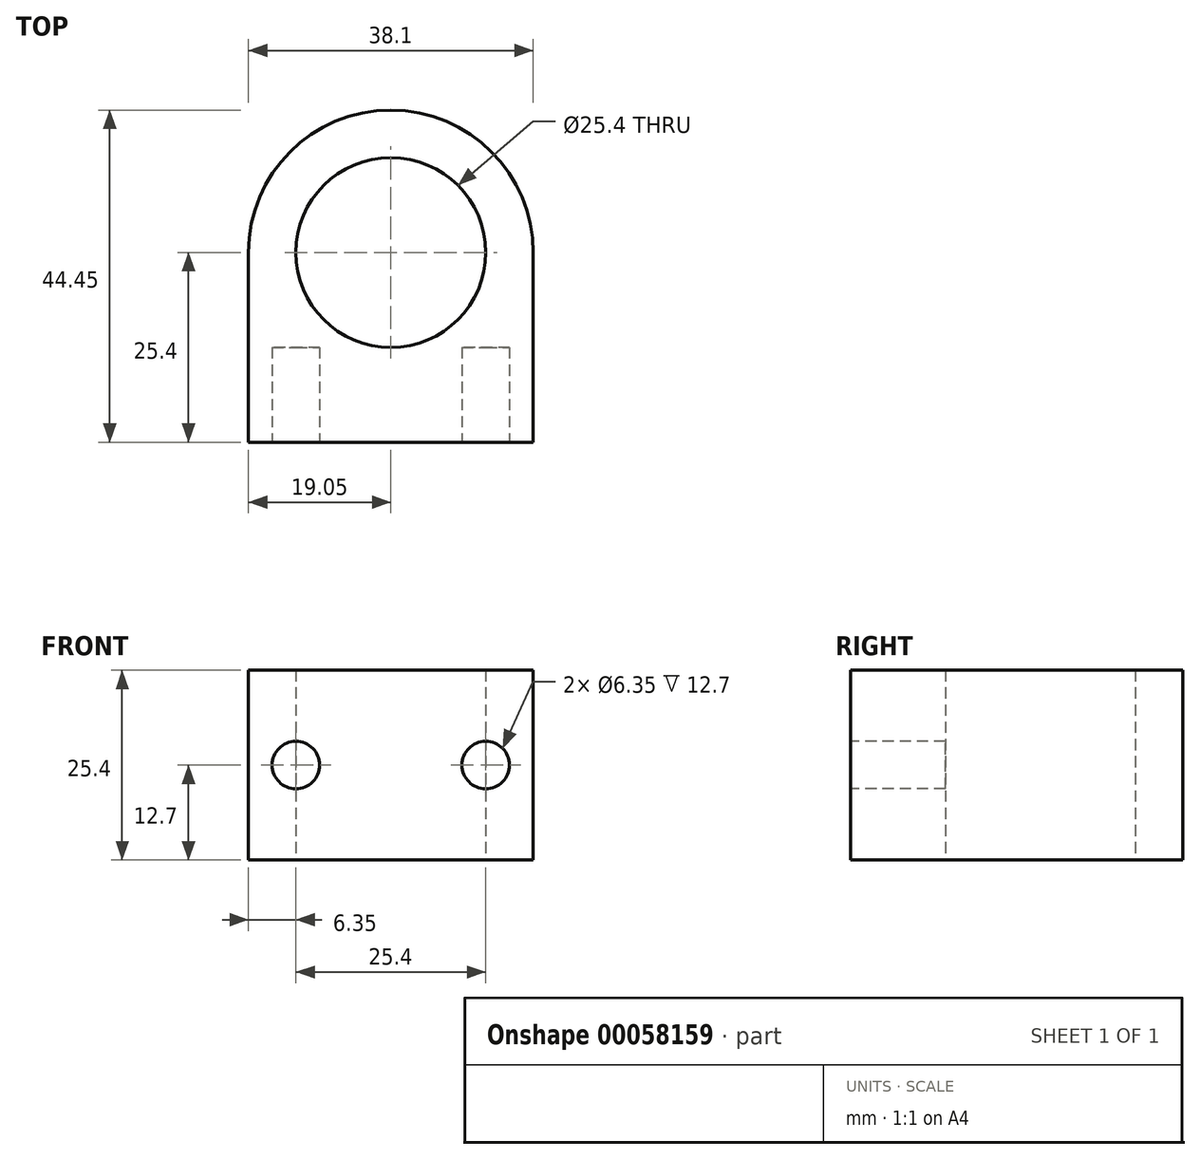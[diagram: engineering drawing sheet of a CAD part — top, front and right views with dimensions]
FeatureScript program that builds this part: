
annotation { "Feature Type Name" : "Feature", "Feature Type Description" : "" }
export const myFeature = defineFeature(function(context is Context, id is Id, definition is map)
    precondition{}
    {
        {
            var Q0;
            Q0=qCreatedBy(makeId("Top.planeOp"),FACE);
            var sketch = newSketch(context, id + "F0", { "sketchPlane" : qUnion([Q0])});
            skCircle(sketch, "E0", {"center": v(0, 0) * mm, "radius": 12.7 * mm});
            skArc(sketch, "E1", {"start": v(19.05, 0) * mm, "mid": v(0, 19.05) * mm, "end": v(-19.05, 0) * mm});
            skLineSegment(sketch, "E2", {"start": v(-19.05, 0) * mm, "end": v(-19.05, -25.4) * mm});
            skLineSegment(sketch, "E3", {"start": v(-19.05, -25.4) * mm, "end": v(19.05, -25.4) * mm});
            skLineSegment(sketch, "E4", {"start": v(19.05, -25.4) * mm, "end": v(19.05, 0) * mm});
            skSolve(sketch);
        }
        {
            var Q0;
            Q0=makeQuery(id+"F0.imprint","IMPRINT",FACE,{"disambiguationData":[TD([[makeQuery(id+"F0.imprint","IMPRINT",EDGE,{"derivedFrom":sQuery(id+"F0.wireOp",EDGE,"E0")}),-1.0]])]});
            extrude(context, id + "F1", {"entities" : qUnion([Q0]), "depth" : 25.4 * mm});
        }
        {
            var Q0;
            Q0=makeQuery(id+"F1.opExtrude","SWEPT_FACE",FACE,{"disambiguationData":[OSD([sQuery(id+"F0.wireOp",EDGE,"E3")])]});
            var sketch = newSketch(context, id + "F2", { "sketchPlane" : qUnion([Q0])});
            skCircle(sketch, "E5", {"center": v(-12.7, 12.7) * mm, "radius": 3.18 * mm});
            skPoint(sketch, "E5.centerSnap0", {"position": v(-19.05, 12.7) * mm});
            skCircle(sketch, "E6", {"center": v(12.7, 12.7) * mm, "radius": 3.18 * mm});
            skSolve(sketch);
        }
        {
            var Q0;
            Q0=makeQuery(id+"F2.imprint","IMPRINT",FACE,{"disambiguationData":[TD([[makeQuery(id+"F2.imprint","IMPRINT",EDGE,{"derivedFrom":sQuery(id+"F2.wireOp",EDGE,"E5")}),1.0]])]});
            var Q1;
            Q1=makeQuery(id+"F2.imprint","IMPRINT",FACE,{"disambiguationData":[TD([[makeQuery(id+"F2.imprint","IMPRINT",EDGE,{"derivedFrom":sQuery(id+"F2.wireOp",EDGE,"E6")}),1.0]])]});
            extrude(context, id + "F3", {"entities" : qUnion([Q0, Q1]), "operationType" : NewBodyOperationType.REMOVE, "oppositeDirection" : true, "depth" : 12.7 * mm});
        }
    });
